# Revit family: SOLA_Hand_Shower_Holder_BP
name_source: partatom
category: Plumbing Fixtures
units: mm (PartAtom-declared; Revit-internal decimal feet)

## family parameters
Always vertical = Yes
Cut with Voids When Loaded = No
Maintain Annotation Orientation = No
OmniClass Number = 23.45.05.14.17
OmniClass Title = Showers
Part Type = Normal
Room Calculation Point = No
Round Connector Dimension = Use Diameter
Shared = No
Work Plane-Based = No

## types (1)
- SOLA Hand Shower Holder And BP - Brushed Brass (SKU 13058)
    CW Connection = No
    Connector_1_Diameter = 21 mm
    Default Elevation = 0 mm  [stored 0 ft]
    Description = SOLA Hand Shower Holder And BP
    HW Connection = No
    Manufacturer = ABI Interiors PTY LTD
    Model = Brushed Brass (SKU 13058)
    URL = https://www.abiinteriors.com.au
    Vent Connection = No
    Waste Connection = No

note: [stored X ft] marks values corroborated as IEEE doubles in the binary element streams (Revit-internal decimal feet)

## geometry (parser evidence)
native form markers: Sweep x3
no freeform markers — native parametric forms only
